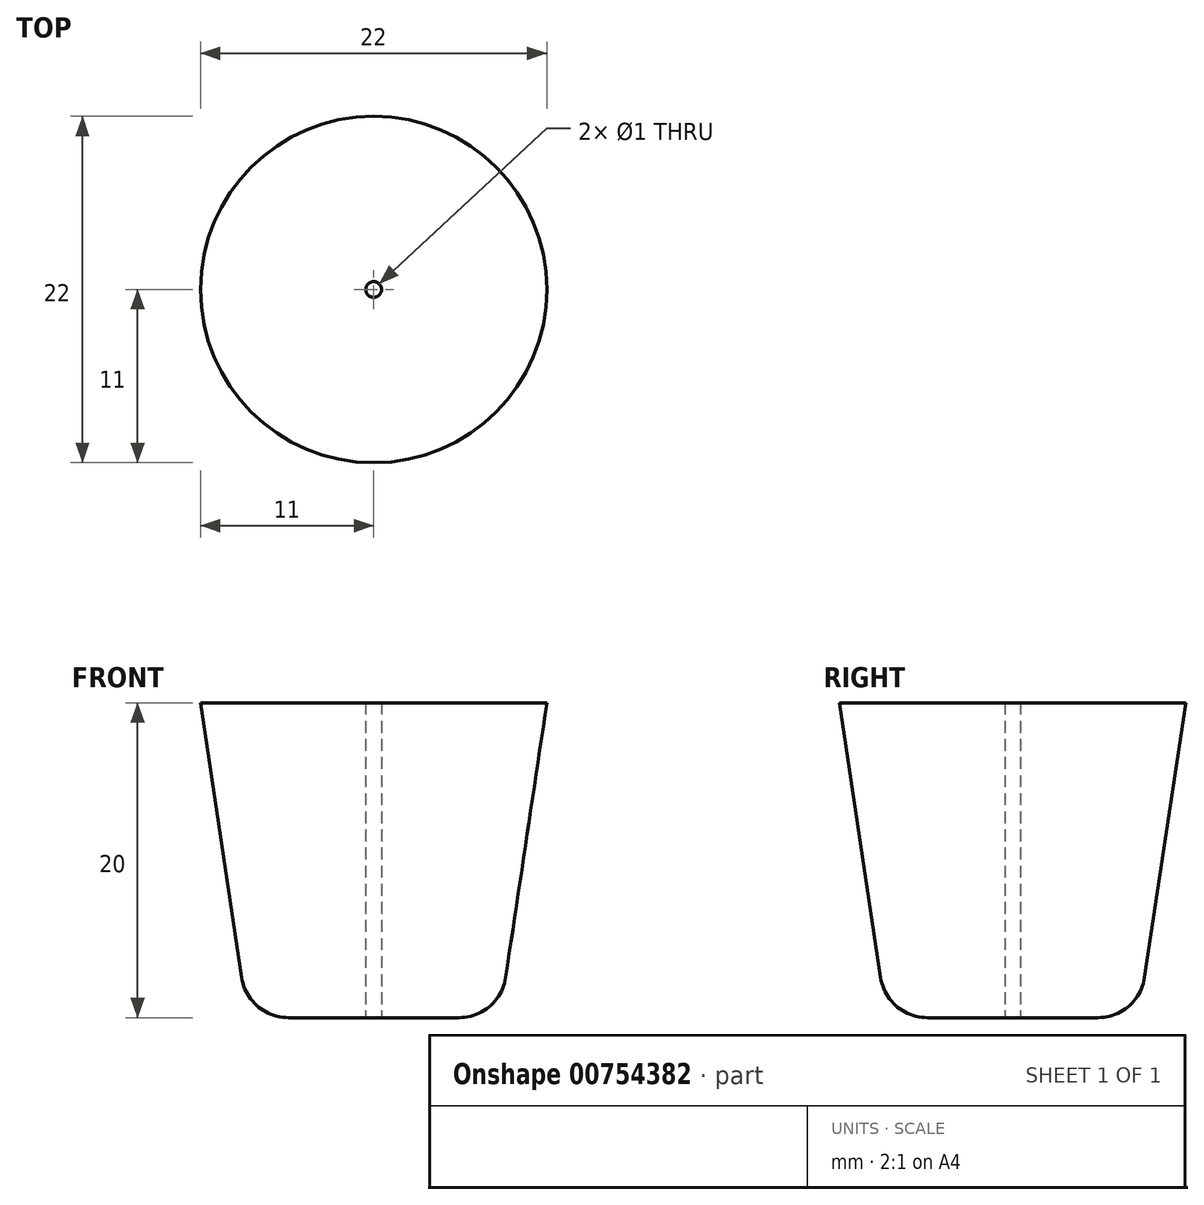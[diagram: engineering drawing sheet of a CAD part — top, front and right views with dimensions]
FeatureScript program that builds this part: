
annotation { "Feature Type Name" : "Feature", "Feature Type Description" : "" }
export const myFeature = defineFeature(function(context is Context, id is Id, definition is map)
    precondition{}
    {
        {
            var Q0;
            Q0=qCreatedBy(makeId("Top.planeOp"),FACE);
            var sketch = newSketch(context, id + "F0", { "sketchPlane" : qUnion([Q0])});
            skCircle(sketch, "E0", {"center": v(0, 0) * mm, "radius": 11 * mm});
            skSolve(sketch);
        }
        {
            var Q0;
            Q0=qCreatedBy(makeId("Top.planeOp"),FACE);
            cPlane(context, id + "F1", {"entities" : qUnion([Q0]), "cplaneType" : CPlaneType.OFFSET, "offset" : 20 * mm, "oppositeDirection" : true, "width" : 150 * mm, "height" : 150 * mm});
        }
        {
            var Q0;
            Q0=qCreatedBy(id+"F1.planeOp",FACE);
            var sketch = newSketch(context, id + "F2", { "sketchPlane" : qUnion([Q0])});
            skCircle(sketch, "E1", {"center": v(0, 0) * mm, "radius": 8 * mm});
            skSolve(sketch);
        }
        {
            var Q0;
            Q0=makeQuery(id+"F0.imprint","IMPRINT",FACE,{"disambiguationData":[TD([[makeQuery(id+"F0.imprint","IMPRINT",EDGE,{"derivedFrom":sQuery(id+"F0.wireOp",EDGE,"E0")}),1.0]])]});
            var Q1;
            Q1=makeQuery(id+"F2.imprint","IMPRINT",FACE,{"disambiguationData":[TD([[makeQuery(id+"F2.imprint","IMPRINT",EDGE,{"derivedFrom":sQuery(id+"F2.wireOp",EDGE,"E1")}),1.0]])]});
            loft(context, id + "F3", {"sheetProfilesArray" : [{ "sheetProfileEntities" : qUnion([Q0]) }, { "sheetProfileEntities" : qUnion([Q1]) }]});
        }
        {
            var Q0;
            Q0=makeQuery(id+"F3.opLoft","MID_CAP_EDGE",EDGE,{"disambiguationData":[OSD([sQuery(id+"F2.wireOp",EDGE,"E1")])],"capPos":1.0});
            fillet(context, id + "F4", {"entities" : qUnion([Q0]), "radius" : 3 * mm, "tangentPropagation" : true, "allowEdgeOverflow" : false});
        }
        {
            var Q0;
            Q0=makeQuery(id+"F3.opLoft","CAP_FACE",FACE,{"disambiguationData":[OSD([makeQuery(id+"F2.imprint","IMPRINT",FACE,{"disambiguationData":[TD([[makeQuery(id+"F2.imprint","IMPRINT",EDGE,{"derivedFrom":sQuery(id+"F2.wireOp",EDGE,"E1")}),1.0]])]})])],"isStart":true});
            var sketch = newSketch(context, id + "F5", { "sketchPlane" : qUnion([Q0])});
            skCircle(sketch, "E2", {"center": v(0, 0) * mm, "radius": 0.5 * mm});
            skSolve(sketch);
        }
        {
            var Q0;
            Q0=makeQuery(id+"F5.imprint","IMPRINT",FACE,{"disambiguationData":[TD([[makeQuery(id+"F5.imprint","IMPRINT",EDGE,{"derivedFrom":sQuery(id+"F5.wireOp",EDGE,"E2")}),1.0]])]});
            extrude(context, id + "F6", {"entities" : qUnion([Q0]), "operationType" : NewBodyOperationType.REMOVE, "oppositeDirection" : true, "depth" : 20 * mm, "offsetDistance" : 25 * mm});
        }
    });
